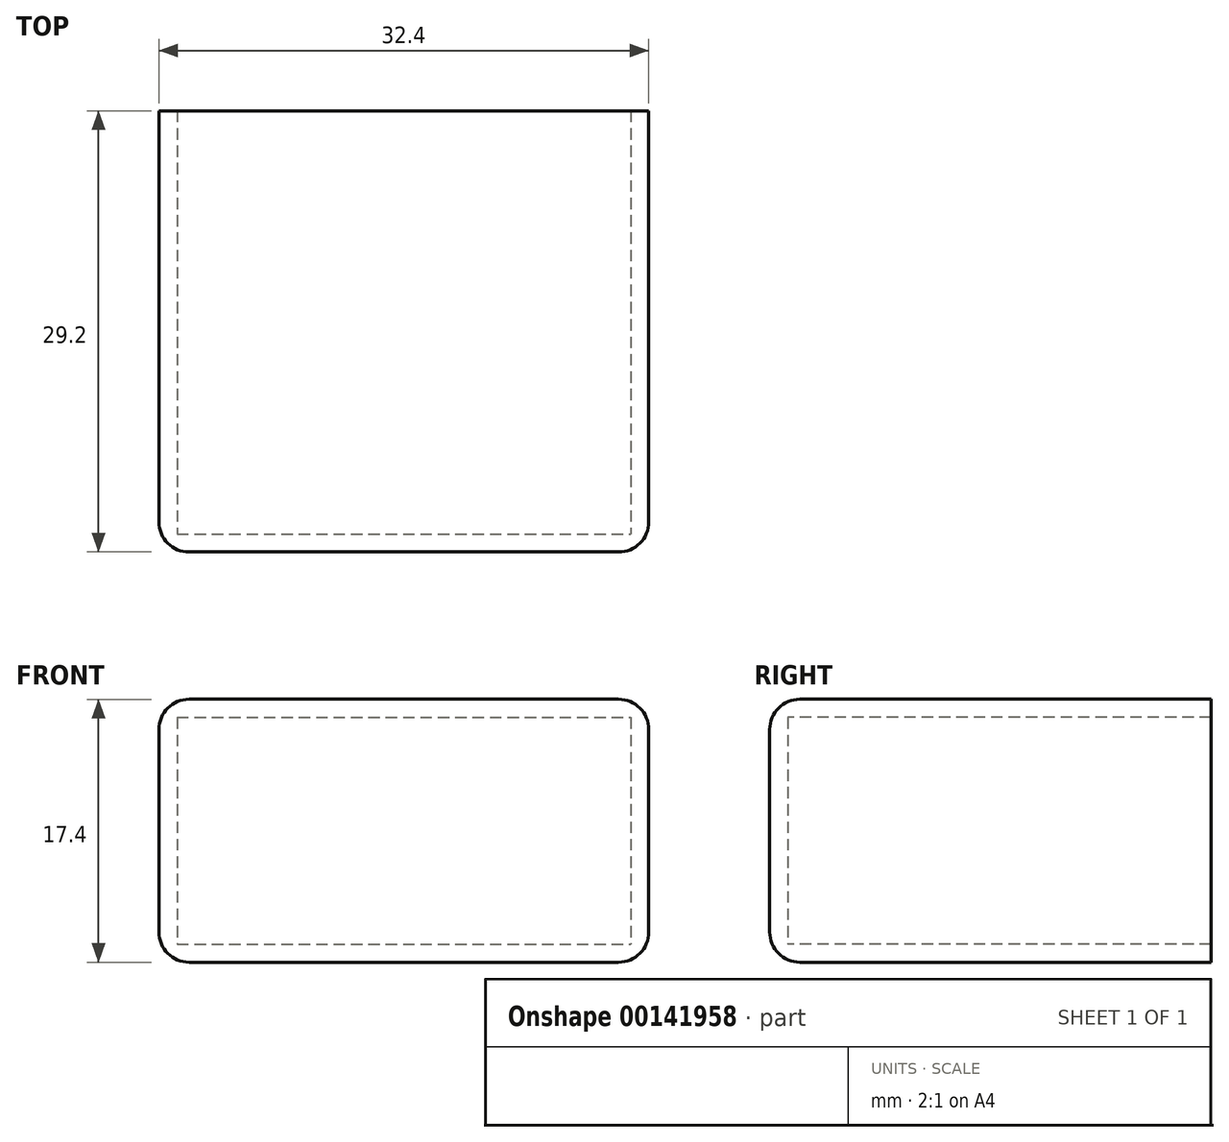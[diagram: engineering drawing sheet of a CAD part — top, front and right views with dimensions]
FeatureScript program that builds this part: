
annotation { "Feature Type Name" : "Feature", "Feature Type Description" : "" }
export const myFeature = defineFeature(function(context is Context, id is Id, definition is map)
    precondition{}
    {
        {
            var Q0;
            Q0=qCreatedBy(makeId("Front.planeOp"),FACE);
            var sketch = newSketch(context, id + "F0", { "sketchPlane" : qUnion([Q0])});
            skLineSegment(sketch, "E0.bottom", {"start": v(-14.15, 0.13) * mm, "end": v(15.85, 0.13) * mm});
            skLineSegment(sketch, "E0.top", {"start": v(-14.15, -14.87) * mm, "end": v(15.85, -14.87) * mm});
            skLineSegment(sketch, "E0.left", {"start": v(-14.15, 0.13) * mm, "end": v(-14.15, -14.87) * mm});
            skLineSegment(sketch, "E0.right", {"start": v(15.85, 0.13) * mm, "end": v(15.85, -14.87) * mm});
            skLineSegment(sketch, "E1.bottom", {"start": v(-15.35, 1.33) * mm, "end": v(17.05, 1.33) * mm});
            skLineSegment(sketch, "E1.top", {"start": v(-15.35, -16.07) * mm, "end": v(17.05, -16.07) * mm});
            skLineSegment(sketch, "E1.left", {"start": v(-15.35, 1.33) * mm, "end": v(-15.35, -16.07) * mm});
            skLineSegment(sketch, "E1.right", {"start": v(17.05, 1.33) * mm, "end": v(17.05, -16.07) * mm});
            skSolve(sketch);
        }
        {
            var Q0;
            Q0=makeQuery(id+"F0.imprint","IMPRINT",FACE,{"disambiguationData":[TD([[makeQuery(id+"F0.imprint","IMPRINT",EDGE,{"derivedFrom":sQuery(id+"F0.wireOp",EDGE,"E0.bottom")}),-1.0]])]});
            extrude(context, id + "F1", {"entities" : qUnion([Q0]), "oppositeDirection" : true, "depth" : 1.2 * mm});
        }
        {
            var Q0;
            Q0=makeQuery(id+"F0.imprint","IMPRINT",FACE,{"disambiguationData":[TD([[makeQuery(id+"F0.imprint","IMPRINT",EDGE,{"derivedFrom":sQuery(id+"F0.wireOp",EDGE,"E0.bottom")}),1.0]])]});
            extrude(context, id + "F2", {"entities" : qUnion([Q0]), "operationType" : NewBodyOperationType.ADD, "oppositeDirection" : true, "depth" : 29.2 * mm});
        }
        {
            var Q0;
            Q0=makeQuery(id+"F2.opExtrude","SWEPT_EDGE",EDGE,{"disambiguationData":[OSD([sQuery(id+"F0.wireOp",EDGE,"E1.bottom"),sQuery(id+"F0.wireOp",EDGE,"E1.right")])]});
            var Q1;
            Q1=makeQuery(id+"F2.opExtrude","CAP_EDGE",EDGE,{"disambiguationData":[OSD([sQuery(id+"F0.wireOp",EDGE,"E1.bottom")])],"isStart":true});
            var Q2;
            Q2=makeQuery(id+"F2.opExtrude","CAP_EDGE",EDGE,{"disambiguationData":[OSD([sQuery(id+"F0.wireOp",EDGE,"E1.top")])],"isStart":true});
            var Q3;
            Q3=makeQuery(id+"F2.opExtrude","CAP_EDGE",EDGE,{"disambiguationData":[OSD([sQuery(id+"F0.wireOp",EDGE,"E1.right")])],"isStart":true});
            var Q4;
            Q4=makeQuery(id+"F2.opExtrude","SWEPT_EDGE",EDGE,{"disambiguationData":[OSD([sQuery(id+"F0.wireOp",EDGE,"E1.top"),sQuery(id+"F0.wireOp",EDGE,"E1.right")])]});
            var Q5;
            Q5=makeQuery(id+"F2.opExtrude","CAP_EDGE",EDGE,{"disambiguationData":[OSD([sQuery(id+"F0.wireOp",EDGE,"E1.left")])],"isStart":true});
            var Q6;
            Q6=makeQuery(id+"F2.opExtrude","SWEPT_EDGE",EDGE,{"disambiguationData":[OSD([sQuery(id+"F0.wireOp",EDGE,"E1.bottom"),sQuery(id+"F0.wireOp",EDGE,"E1.left")])]});
            var Q7;
            Q7=makeQuery(id+"F2.opExtrude","SWEPT_EDGE",EDGE,{"disambiguationData":[OSD([sQuery(id+"F0.wireOp",EDGE,"E1.top"),sQuery(id+"F0.wireOp",EDGE,"E1.left")])]});
            fillet(context, id + "F3", {"entities" : qUnion([Q0, Q1, Q2, Q3, Q4, Q5, Q6, Q7]), "radius" : 2 * mm, "tangentPropagation" : true, "allowEdgeOverflow" : false});
        }
    });
